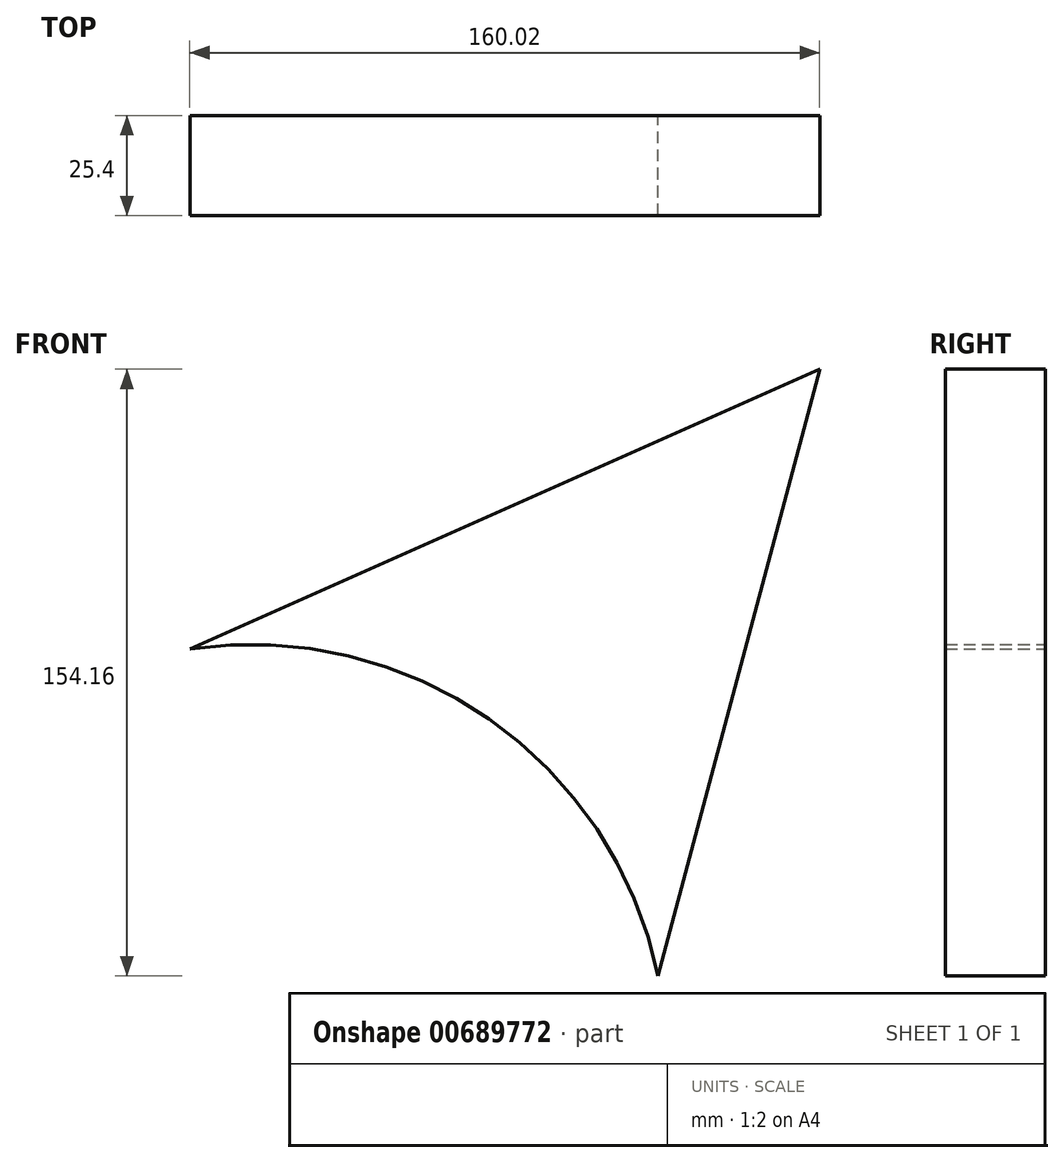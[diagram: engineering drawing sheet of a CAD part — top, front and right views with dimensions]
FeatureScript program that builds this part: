
annotation { "Feature Type Name" : "Feature", "Feature Type Description" : "" }
export const myFeature = defineFeature(function(context is Context, id is Id, definition is map)
    precondition{}
    {
        {
            var Q0;
            Q0=qCreatedBy(makeId("Front.planeOp"),FACE);
            var sketch = newSketch(context, id + "F0", { "sketchPlane" : qUnion([Q0])});
            skLineSegment(sketch, "E0", {"start": v(65.72, 71.14) * mm, "end": v(-94.3, 0) * mm});
            skLineSegment(sketch, "E1", {"start": v(65.72, 71.14) * mm, "end": v(24.68, -83.02) * mm});
            skArc(sketch, "E2", {"start": v(24.68, -83.02) * mm, "mid": v(-18.27, -17.8) * mm, "end": v(-94.3, 0) * mm});
            skSolve(sketch);
        }
        {
            var Q0;
            Q0 = qSketchRegion(id + "F0", true);
            extrude(context, id + "F1", {"entities" : qUnion([Q0]), "depth" : 25.4 * mm, "offsetDistance" : 25.4 * mm});
        }
    });
